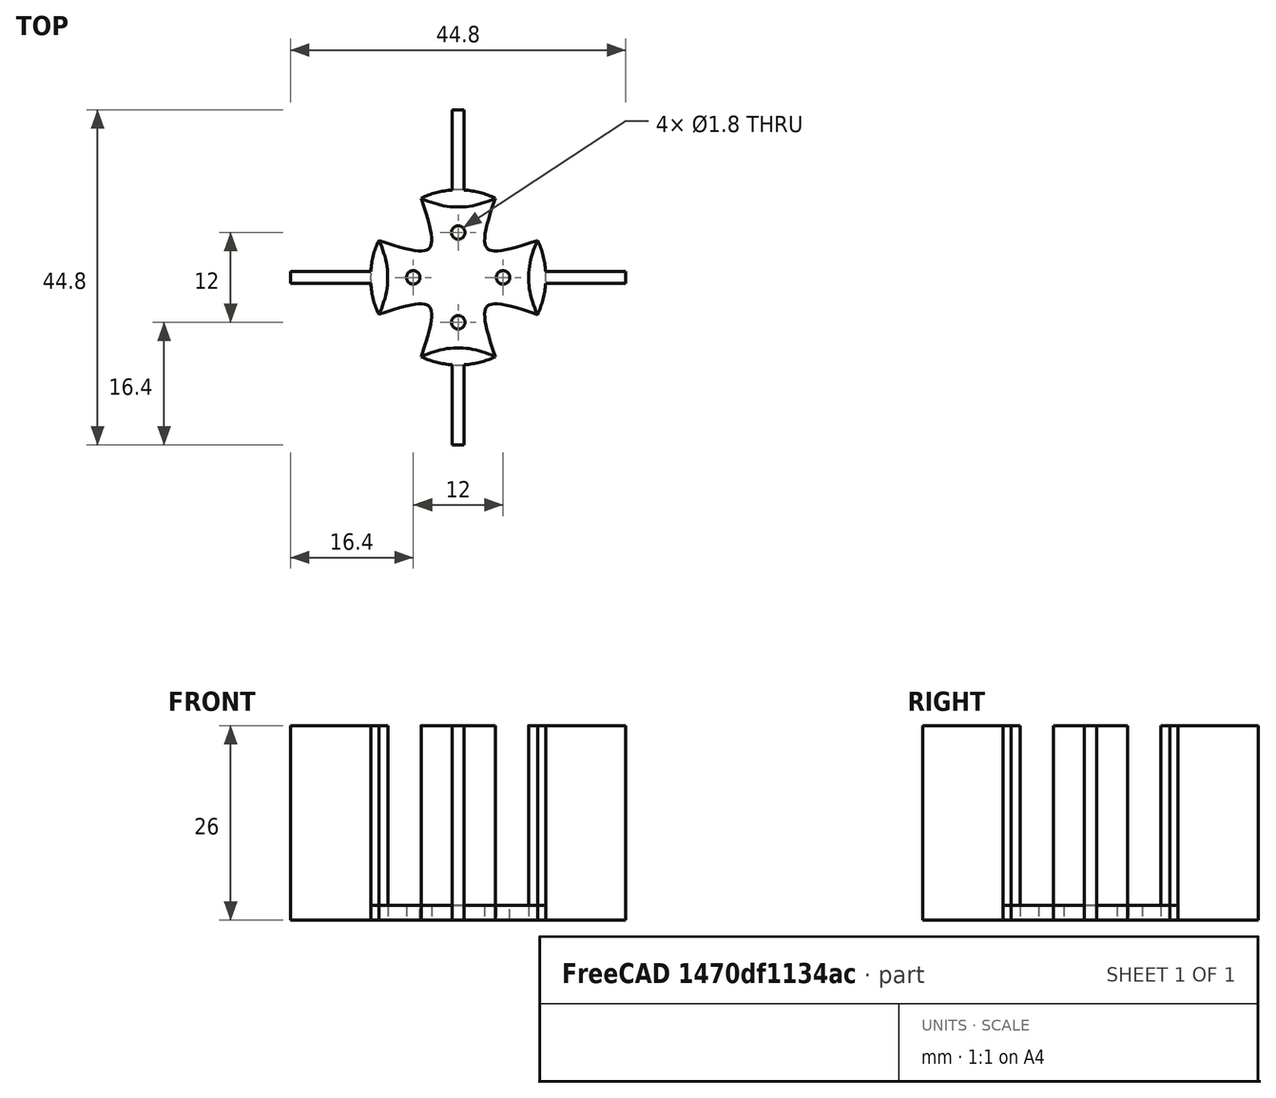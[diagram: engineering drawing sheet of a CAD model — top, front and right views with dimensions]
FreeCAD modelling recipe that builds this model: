
FCSTD DOCUMENT  (FreeCAD 0.19R0.19.2)
Label: boatMoterHolder012
License: All rights reserved
LicenseURL: http://en.wikipedia.org/wiki/All_rights_reserved
objects: Sketcher::SketchObject×2, Part::Extrusion×2
note: 4 computed .brp shape members not serialized (recipe doc carries the construction recipe); baked Part::Feature solids carry a one-line shape summary decoded from their .brp

FEATURE [Sketcher::SketchObject] Sketch
  FullyConstrained = true
  sketch-geometry (44):
    g0: Circle CenterX=-6 CenterY=0 CenterZ=0 NormalX=0 NormalY=0 NormalZ=1 AngleXU=0 Radius=0.9
    g1: Circle CenterX=0 CenterY=6 CenterZ=0 NormalX=0 NormalY=0 NormalZ=1 AngleXU=0 Radius=0.9
    g2: Circle CenterX=6 CenterY=0 CenterZ=0 NormalX=0 NormalY=0 NormalZ=1 AngleXU=0 Radius=0.9
    g3: Circle CenterX=0 CenterY=-6 CenterZ=0 NormalX=0 NormalY=0 NormalZ=1 AngleXU=0 Radius=0.9
    g4-g8: Circle x5 (B-spline internal-alignment scaffolding for g9; pole/knot coordinates omitted)
    g9: BSplineCurve PolesCount=5 KnotsCount=3 Degree=3 IsPeriodic=0
    g10: GeomPoint X=-4.94974 Y=10.6066 Z=0
    g11: GeomPoint X=-3.88908 Y=3.88909 Z=0
    g12: GeomPoint X=-10.6066 Y=4.94975 Z=0
    g13-g17: Circle x5 (B-spline internal-alignment scaffolding for g18; pole/knot coordinates omitted)
    g18: BSplineCurve PolesCount=5 KnotsCount=3 Degree=3 IsPeriodic=0
    g19: GeomPoint X=-10.6066 Y=-4.94974 Z=0
    g20: GeomPoint X=-3.88212 Y=-3.88197 Z=0
    g21: GeomPoint X=-4.94053 Y=-10.6109 Z=0
    g22-g26: Circle x5 (B-spline internal-alignment scaffolding for g27; pole/knot coordinates omitted)
    g27: BSplineCurve PolesCount=5 KnotsCount=3 Degree=3 IsPeriodic=0
    g28: GeomPoint X=4.94975 Y=-10.6066 Z=0
    g29: GeomPoint X=3.8852 Y=-3.88525 Z=0
    g30: GeomPoint X=10.603 Y=-4.95737 Z=0
    g31-g35: Circle x5 (B-spline internal-alignment scaffolding for g36; pole/knot coordinates omitted)
    g36: BSplineCurve PolesCount=5 KnotsCount=3 Degree=3 IsPeriodic=0
    g37: GeomPoint X=10.6066 Y=4.94975 Z=0
    g38: GeomPoint X=3.8891 Y=3.88908 Z=0
    g39: GeomPoint X=4.94975 Y=10.6066 Z=0
    g40: ArcOfCircle CenterX=0 CenterY=0 CenterZ=0 NormalX=0 NormalY=0 NormalZ=1 AngleXU=0 Radius=11.7047 StartAngle=1.13417 EndAngle=2.00742
    g41: ArcOfCircle CenterX=0 CenterY=0 CenterZ=0 NormalX=0 NormalY=0 NormalZ=1 AngleXU=0 Radius=11.7047 StartAngle=5.84584 EndAngle=6.71981
    g42: ArcOfCircle CenterX=0 CenterY=0 CenterZ=0 NormalX=0 NormalY=0 NormalZ=1 AngleXU=0 Radius=11.7047 StartAngle=4.27663 EndAngle=5.14902
    g43: ArcOfCircle CenterX=0 CenterY=0 CenterZ=0 NormalX=0 NormalY=0 NormalZ=1 AngleXU=0 Radius=11.7047 StartAngle=2.70497 EndAngle=3.57822
  constraints (50):
    c: Block(g1)
    c: Block(g2)
    c: Block(g3)
    c: Block(g0)
    c: Weight(g4) = 1
    c: Equal(g4, g5-g8) x4
    c: InternalAlignment(g4-g8 -> g9) x5
    c: InternalAlignment(g10,g9)
    c: InternalAlignment(g11,g9)
    c: InternalAlignment(g12,g9)
    c: Weight(g13) = 1
    c: Equal(g13, g14-g17) x4
    c: InternalAlignment(g13-g17 -> g18) x5
    c: InternalAlignment(g19,g18)
    c: InternalAlignment(g20,g18)
    c: InternalAlignment(g21,g18)
    c: Weight(g22) = 1
    c: Equal(g22,g24)
    c: Equal(g22,g25)
    c: Equal(g22,g26)
    c: InternalAlignment(g22-g26 -> g27) x5
    c: InternalAlignment(g28,g27)
    c: InternalAlignment(g29,g27)
    c: InternalAlignment(g30,g27)
    c: Weight(g31) = 1
    c: Equal(g31, g32-g35) x4
    c: InternalAlignment(g31-g35 -> g36) x5
    c: InternalAlignment(g37,g36)
    c: InternalAlignment(g38,g36)
    c: InternalAlignment(g39,g36)
    c: Coincident(g40,g-1)
    c: Coincident(g40,g9)
    c: Coincident(g40,g36)
    c: Coincident(g41,g40)
    c: Coincident(g41,g36)
    c: Coincident(g41,g27)
    c: Coincident(g42,g40)
    c: Coincident(g42,g27)
    c: Coincident(g42,g18)
    c: Coincident(g43,g40)
    c: Coincident(g43,g18)
    c: Coincident(g43,g9)
    c: Block(g41)
    c: Block(g40)
    c: Block(g43)
    c: Block(g42)
    c: Block(g36)
    c: Block(g9)
    c: Block(g27)
    c: Block(g18)
FEATURE [Part::Extrusion] Extrude
  Base = -> Sketch
  Dir = (0,0,1)
  DirMode = 2
  FaceMakerClass = Part::FaceMakerBullseye
  LengthFwd = 2
  LengthRev = 0
  Solid = true
  Symmetric = false
FEATURE [Sketcher::SketchObject] Sketch001
  FullyConstrained = true
  sketch-geometry (44):
    g0: ArcOfCircle CenterX=0 CenterY=0 CenterZ=0 NormalX=0 NormalY=0 NormalZ=1 AngleXU=0 Radius=11.7047 StartAngle=1.13417 EndAngle=1.50239
    g1: ArcOfCircle CenterX=0 CenterY=0 CenterZ=0 NormalX=0 NormalY=0 NormalZ=1 AngleXU=0 Radius=11.7047 StartAngle=5.84584 EndAngle=6.21478
    g2: ArcOfCircle CenterX=0 CenterY=0 CenterZ=0 NormalX=0 NormalY=0 NormalZ=1 AngleXU=0 Radius=11.7047 StartAngle=4.27663 EndAngle=4.64399
    g3: ArcOfCircle CenterX=0 CenterY=0 CenterZ=0 NormalX=0 NormalY=0 NormalZ=1 AngleXU=0 Radius=11.7047 StartAngle=2.70497 EndAngle=3.07319
    g4: LineSegment StartX=22.4 StartY=-0.8 StartZ=0 EndX=11.6773 EndY=-0.8 EndZ=0
    g5: LineSegment StartX=22.4 StartY=0.8 StartZ=0 EndX=11.6773 EndY=0.8 EndZ=0
    g6: LineSegment StartX=0.8 StartY=22.4 StartZ=0 EndX=0.8 EndY=11.6773 EndZ=0
    g7: LineSegment StartX=-0.8 StartY=22.4 StartZ=0 EndX=-0.8 EndY=11.6773 EndZ=0
    g8: LineSegment StartX=-22.4 StartY=0.8 StartZ=0 EndX=-11.6773 EndY=0.8 EndZ=0
    g9: LineSegment StartX=-22.4 StartY=-0.8 StartZ=0 EndX=-11.6773 EndY=-0.8 EndZ=0
    g10: LineSegment StartX=-22.4 StartY=0.8 StartZ=0 EndX=-22.4 EndY=-0.8 EndZ=0
    g11: ArcOfCircle CenterX=0 CenterY=0 CenterZ=0 NormalX=0 NormalY=0 NormalZ=1 AngleXU=0 Radius=11.7047 StartAngle=3.20999 EndAngle=3.57822
    g12: ArcOfCircle CenterX=0 CenterY=0 CenterZ=0 NormalX=0 NormalY=0 NormalZ=1 AngleXU=0 Radius=11.7047 StartAngle=1.6392 EndAngle=2.00742
    g13: ArcOfCircle CenterX=0 CenterY=0 CenterZ=0 NormalX=0 NormalY=0 NormalZ=1 AngleXU=0 Radius=11.7047 StartAngle=0.0684019 EndAngle=0.436627
    g14: LineSegment StartX=-0.8 StartY=22.4 StartZ=0 EndX=0.8 EndY=22.4 EndZ=0
    g15: LineSegment StartX=22.4 StartY=-0.8 StartZ=0 EndX=22.4 EndY=0.8 EndZ=0
    g16: LineSegment StartX=0.8 StartY=-22.4 StartZ=0 EndX=0.8 EndY=-11.6773 EndZ=0
    g17: LineSegment StartX=-0.8 StartY=-22.4 StartZ=0 EndX=-0.8 EndY=-11.6773 EndZ=0
    g18: LineSegment StartX=-0.8 StartY=-22.4 StartZ=0 EndX=0.8 EndY=-22.4 EndZ=0
    g19: ArcOfCircle CenterX=0 CenterY=0 CenterZ=0 NormalX=0 NormalY=0 NormalZ=1 AngleXU=0 Radius=11.7047 StartAngle=4.78079 EndAngle=5.14902
    g20: Circle CenterX=-10.6066 CenterY=4.94975 CenterZ=0 NormalX=0 NormalY=0 NormalZ=1 AngleXU=0 Radius=1
    g21: Circle CenterX=-8.2 CenterY=0 CenterZ=0 NormalX=0 NormalY=0 NormalZ=1 AngleXU=0 Radius=1
    g22: Circle CenterX=-10.6066 CenterY=-4.94974 CenterZ=0 NormalX=0 NormalY=0 NormalZ=1 AngleXU=0 Radius=1
    g23: BSplineCurve PolesCount=3 KnotsCount=2 Degree=2 IsPeriodic=0
    g24: GeomPoint X=-10.6066 Y=4.94975 Z=0
    g25: GeomPoint X=-10.6066 Y=-4.94974 Z=0
    g26: Circle CenterX=-4.94974 CenterY=10.6066 CenterZ=0 NormalX=0 NormalY=0 NormalZ=1 AngleXU=0 Radius=1
    g27: Circle CenterX=0 CenterY=8.2 CenterZ=0 NormalX=0 NormalY=0 NormalZ=1 AngleXU=0 Radius=1
    g28: Circle CenterX=4.94975 CenterY=10.6066 CenterZ=0 NormalX=0 NormalY=0 NormalZ=1 AngleXU=0 Radius=1
    g29: BSplineCurve PolesCount=3 KnotsCount=2 Degree=2 IsPeriodic=0
    g30: GeomPoint X=-4.94974 Y=10.6066 Z=0
    g31: GeomPoint X=4.94975 Y=10.6066 Z=0
    g32: Circle CenterX=10.6066 CenterY=4.94975 CenterZ=0 NormalX=0 NormalY=0 NormalZ=1 AngleXU=0 Radius=1
    g33: Circle CenterX=8.2 CenterY=0 CenterZ=0 NormalX=0 NormalY=0 NormalZ=1 AngleXU=0 Radius=1
    g34: Circle CenterX=10.603 CenterY=-4.95737 CenterZ=0 NormalX=0 NormalY=0 NormalZ=1 AngleXU=0 Radius=1
    g35: BSplineCurve PolesCount=3 KnotsCount=2 Degree=2 IsPeriodic=0
    g36: GeomPoint X=10.6066 Y=4.94975 Z=0
    g37: GeomPoint X=10.603 Y=-4.95737 Z=0
    g38: Circle CenterX=4.94975 CenterY=-10.6066 CenterZ=0 NormalX=0 NormalY=0 NormalZ=1 AngleXU=0 Radius=1
    g39: Circle CenterX=0 CenterY=-8.2 CenterZ=0 NormalX=0 NormalY=0 NormalZ=1 AngleXU=0 Radius=1
    g40: Circle CenterX=-4.94053 CenterY=-10.6109 CenterZ=0 NormalX=0 NormalY=0 NormalZ=1 AngleXU=0 Radius=1
    g41: BSplineCurve PolesCount=3 KnotsCount=2 Degree=2 IsPeriodic=0
    g42: GeomPoint X=4.94975 Y=-10.6066 Z=0
    g43: GeomPoint X=-4.94053 Y=-10.6109 Z=0
  constraints (106):
    c: Coincident(g0,g-1)
    c: Coincident(g1,g0)
    c: Coincident(g2,g0)
    c: Coincident(g3,g0)
    c: Block(g1)
    c: Block(g0)
    c: Block(g3)
    c: Block(g2)
    c: Horizontal(g4)
    c: Horizontal(g5)
    c: Vertical(g6)
    c: Vertical(g7)
    c: Horizontal(g8)
    c: Horizontal(g9)
    c: Block(g9)
    c: Block(g8)
    c: Block(g7)
    c: Block(g6)
    c: Block(g5)
    c: Block(g4)
    c: Coincident(g10,g8)
    c: Coincident(g10,g9)
    c: Vertical(g10)
    c: Distance(g10) = 1.6
    c: Equal(g3,g11)
    c: Coincident(g3,g8)
    c: Coincident(g11,g9)
    c: Coincident(g3,g11)
    c: Equal(g0,g12)
    c: Coincident(g0,g6)
    c: Coincident(g12,g7)
    c: Coincident(g0,g12)
    c: Equal(g1,g13)
    c: Coincident(g1,g4)
    c: PointOnObject(g13,g5)
    c: Coincident(g1,g13)
    c: Coincident(g14,g7)
    c: Coincident(g14,g6)
    c: Horizontal(g14)
    c: Distance(g14) = 1.6
    c: Coincident(g15,g4)
    c: Coincident(g15,g5)
    c: Vertical(g15)
    c: Distance(g15) = 1.6
    c: Vertical(g16)
    c: Vertical(g17)
    c: Block(g16)
    c: Block(g17)
    c: Coincident(g18,g17)
    c: Coincident(g18,g16)
    c: Horizontal(g18)
    c: Equal(g2,g19)
    c: Coincident(g2,g17)
    c: Coincident(g19,g16)
    c: Coincident(g2,g19)
    c: Block(g11)
    c: Block(g12)
    c: Block(g13)
    c: Block(g19)
    c: PointOnObject(g21,g-1)
    c: PointOnObject(g33,g-1)
    c: PointOnObject(g39,g-2)
    c: Coincident(g23,g3)
    c: Weight(g20) = 1
    c: Equal(g20,g21)
    c: Equal(g20,g22)
    c: Coincident(g23,g11)
    c: InternalAlignment(g20,g23)
    c: InternalAlignment(g21,g23)
    c: InternalAlignment(g22,g23)
    c: InternalAlignment(g24,g23)
    c: InternalAlignment(g25,g23)
    c: Coincident(g29,g12)
    c: Weight(g26) = 1
    c: Equal(g26,g27)
    c: Equal(g26,g28)
    c: Coincident(g29,g0)
    c: InternalAlignment(g26,g29)
    c: InternalAlignment(g27,g29)
    c: InternalAlignment(g28,g29)
    c: InternalAlignment(g30,g29)
    c: InternalAlignment(g31,g29)
    c: Coincident(g35,g13)
    c: Weight(g32) = 1
    c: Equal(g32,g33)
    c: Equal(g32,g34)
    c: Coincident(g35,g1)
    c: InternalAlignment(g32,g35)
    c: InternalAlignment(g33,g35)
    c: InternalAlignment(g34,g35)
    c: InternalAlignment(g36,g35)
    c: InternalAlignment(g37,g35)
    c: Coincident(g41,g19)
    c: Weight(g38) = 1
    c: Equal(g38,g39)
    c: Equal(g38,g40)
    c: Coincident(g41,g2)
    c: InternalAlignment(g38,g41)
    c: InternalAlignment(g39,g41)
    c: InternalAlignment(g40,g41)
    c: InternalAlignment(g42,g41)
    c: InternalAlignment(g43,g41)
    c: Block(g29)
    c: Block(g23)
    c: Block(g35)
    c: Block(g41)
FEATURE [Part::Extrusion] Extrude001
  Base = -> Sketch001
  Dir = (0,0,1)
  DirMode = 2
  FaceMakerClass = Part::FaceMakerBullseye
  LengthFwd = 26
  LengthRev = 0
  Solid = true
  Symmetric = false
